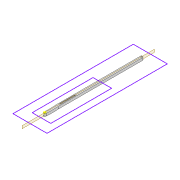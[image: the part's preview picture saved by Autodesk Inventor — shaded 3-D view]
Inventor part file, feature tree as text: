
AUTODESK INVENTOR PART (.ipt)
format: ipt  version: 2022 (Build 260153000, 153)  size: 118,784 bytes
history: native  units: mm
features: sketch x3, extrude x1, projected_geometry x1
ambient origin geometry x8: Origin, YZ Plane, XZ Plane, XY Plane, X Axis, Y Axis, Z Axis, Center Point
bodies: Solid1 (feature_tree)
feature tree (5):
  extrude  "Extrusion1"  Depth=8.0mm
  sketch  "Sketch2"  dims[d2=3.0mm]
  sketch  "Sketch3"  dims[d3=3.0mm d4=8.0mm d5=0.0mm d12=3.0mm d13=50.8mm d14=100.0mm d15=40.0mm d16=200.0mm d17=200.0mm d18=0.5mm d19=0.872665mm d20=0.5mm d21=0.872665mm]
  sketch  "Sketch1"  dims[d0=319.927mm d1=8.0mm]
  projected_geometry  "Projected Loop1"
